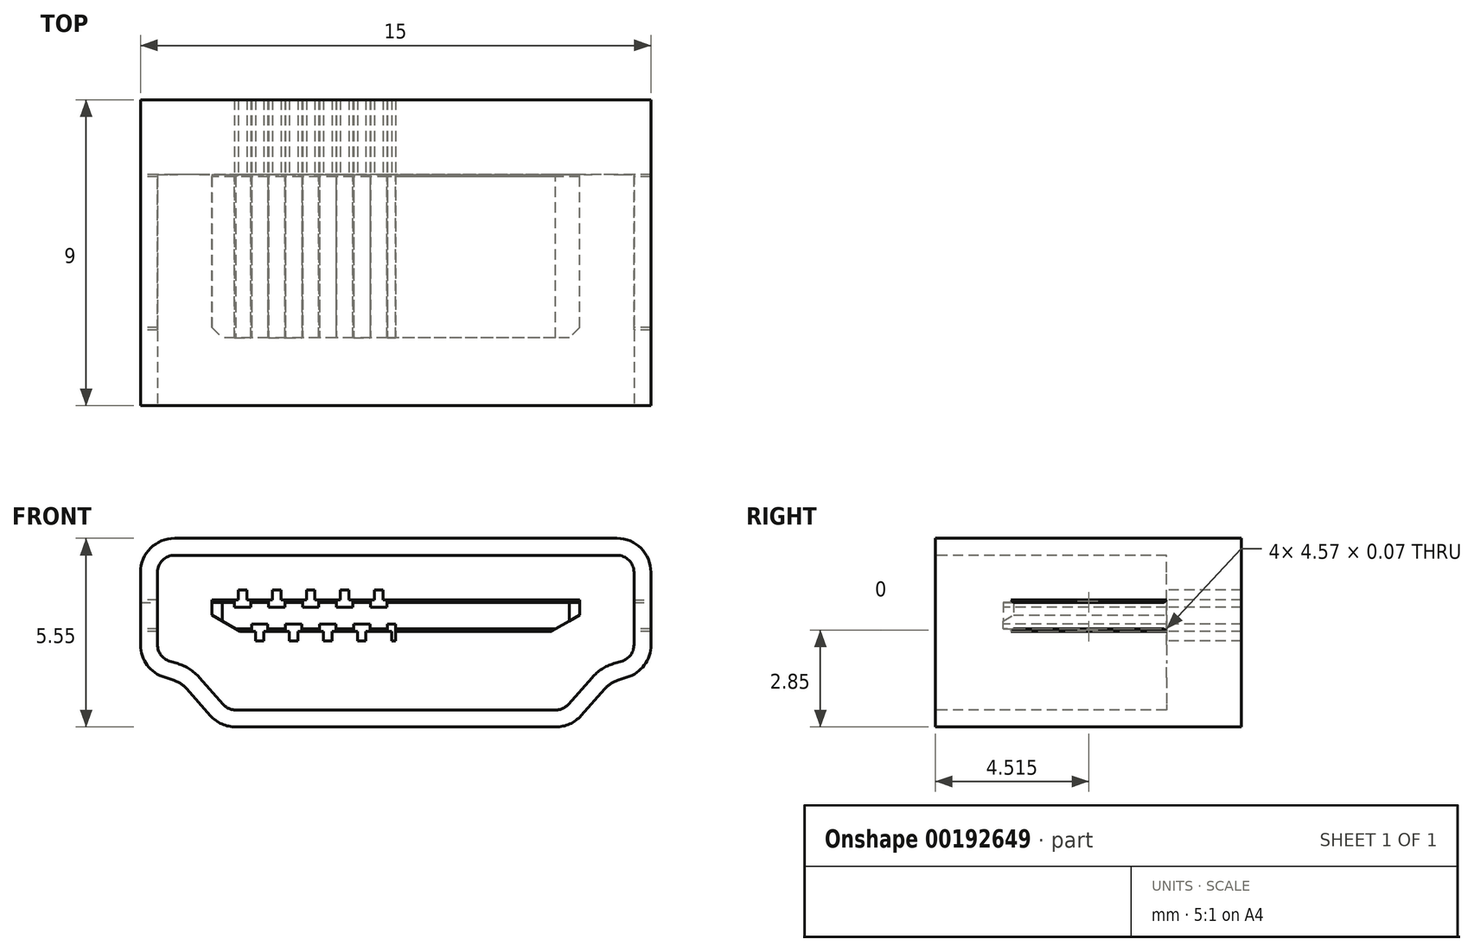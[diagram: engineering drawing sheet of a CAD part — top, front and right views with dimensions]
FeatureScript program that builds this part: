
annotation { "Feature Type Name" : "Feature", "Feature Type Description" : "" }
export const myFeature = defineFeature(function(context is Context, id is Id, definition is map)
    precondition{}
    {
        {
            var Q0;
            Q0=qCreatedBy(makeId("Front.planeOp"),FACE);
            var sketch = newSketch(context, id + "F0", { "sketchPlane" : qUnion([Q0])});
            skLineSegment(sketch, "E0", {"start": v(-6.5, 5.55) * mm, "end": v(7.5, 5.55) * mm});
            skLineSegment(sketch, "E1", {"start": v(-4.7, 0) * mm, "end": v(4.7, 0) * mm});
            skLineSegment(sketch, "E2", {"start": v(-7.5, 4.55) * mm, "end": v(-7.5, 2.42) * mm});
            skPoint(sketch, "E3.visualSharp", {"position": v(-7.5, 5.55) * mm});
            skArc(sketch, "E3.filletArc", {"start": v(-6.5, 5.55) * mm, "mid": v(-7.2, 5.26) * mm, "end": v(-7.5, 4.55) * mm});
            skArc(sketch, "E4", {"start": v(-7.5, 2.42) * mm, "mid": v(-7.3, 1.82) * mm, "end": v(-6.8, 1.46) * mm});
            skLineSegment(sketch, "E5", {"start": v(-6.8, 1.46) * mm, "end": v(-6.56, 1.39) * mm});
            skArc(sketch, "E6", {"start": v(-5.45, 0.34) * mm, "mid": v(-5.11, 0.09) * mm, "end": v(-4.7, 0) * mm});
            skLineSegment(sketch, "E7", {"start": v(-5.45, 0.34) * mm, "end": v(-6.14, 1.12) * mm});
            skArc(sketch, "E8", {"start": v(-6.14, 1.12) * mm, "mid": v(-6.33, 1.28) * mm, "end": v(-6.56, 1.39) * mm});
            skLineSegment(sketch, "E9", {"start": v(0, 0) * mm, "end": v(0, 5.55) * mm, "construction": true});
            skLineSegment(sketch, "E10.MirrorCS", {"start": v(6.8, 1.46) * mm, "end": v(6.56, 1.39) * mm});
            skArc(sketch, "E11.MirrorCS", {"start": v(5.45, 0.34) * mm, "mid": v(5.11, 0.09) * mm, "end": v(4.7, 0) * mm});
            skArc(sketch, "E12.MirrorCS", {"start": v(6.14, 1.12) * mm, "mid": v(6.33, 1.28) * mm, "end": v(6.56, 1.39) * mm});
            skLineSegment(sketch, "E13.MirrorCS", {"start": v(5.45, 0.34) * mm, "end": v(6.14, 1.12) * mm});
            skArc(sketch, "E14.MirrorCS", {"start": v(6.5, 5.55) * mm, "mid": v(7.2, 5.26) * mm, "end": v(7.5, 4.55) * mm});
            skArc(sketch, "E15.MirrorCS", {"start": v(7.5, 2.42) * mm, "mid": v(7.3, 1.82) * mm, "end": v(6.8, 1.46) * mm});
            skLineSegment(sketch, "E16.MirrorCS", {"start": v(7.5, 4.55) * mm, "end": v(7.5, 2.42) * mm});
            skSolve(sketch);
        }
        {
            var Q0;
            Q0 = qSketchRegion(id + "F0", true);
            extrude(context, id + "F1", {"entities" : qUnion([Q0]), "endBound" : BoundingType.SYMMETRIC, "depth" : 9 * mm});
        }
        {
            var Q0;
            Q0=makeQuery(id+"F1.opExtrude","CAP_FACE",FACE,{"disambiguationData":[OSD([sQuery(id+"F0.wireOp",EDGE,"E0"),sQuery(id+"F0.wireOp",EDGE,"E1"),sQuery(id+"F0.wireOp",EDGE,"E2"),sQuery(id+"F0.wireOp",EDGE,"E3.filletArc"),sQuery(id+"F0.wireOp",EDGE,"E4"),sQuery(id+"F0.wireOp",EDGE,"E5"),sQuery(id+"F0.wireOp",EDGE,"E6"),sQuery(id+"F0.wireOp",EDGE,"E7"),sQuery(id+"F0.wireOp",EDGE,"E8"),sQuery(id+"F0.wireOp",EDGE,"E10.MirrorCS"),sQuery(id+"F0.wireOp",EDGE,"E11.MirrorCS"),sQuery(id+"F0.wireOp",EDGE,"E12.MirrorCS"),sQuery(id+"F0.wireOp",EDGE,"E13.MirrorCS"),sQuery(id+"F0.wireOp",EDGE,"E14.MirrorCS"),sQuery(id+"F0.wireOp",EDGE,"E15.MirrorCS"),sQuery(id+"F0.wireOp",EDGE,"E16.MirrorCS")])],"isStart":false});
            var sketch = newSketch(context, id + "F2", { "sketchPlane" : qUnion([Q0])});
            skArc(sketch, "E17.0", {"start": v(7, 4.55) * mm, "mid": v(6.85, 4.9) * mm, "end": v(6.5, 5.05) * mm});
            skLineSegment(sketch, "E17.1", {"start": v(7, 2.42) * mm, "end": v(7, 4.55) * mm});
            skArc(sketch, "E17.2", {"start": v(6.65, 1.94) * mm, "mid": v(6.9, 2.12) * mm, "end": v(7, 2.42) * mm});
            skLineSegment(sketch, "E17.3", {"start": v(6.41, 1.87) * mm, "end": v(6.65, 1.94) * mm});
            skArc(sketch, "E17.4", {"start": v(5.77, 1.45) * mm, "mid": v(6.06, 1.7) * mm, "end": v(6.41, 1.87) * mm});
            skLineSegment(sketch, "E17.5", {"start": v(-6.65, 1.94) * mm, "end": v(-6.41, 1.87) * mm});
            skArc(sketch, "E17.6", {"start": v(-7, 2.42) * mm, "mid": v(-6.9, 2.12) * mm, "end": v(-6.65, 1.94) * mm});
            skLineSegment(sketch, "E17.7", {"start": v(-7, 4.55) * mm, "end": v(-7, 2.42) * mm});
            skArc(sketch, "E17.8", {"start": v(-6.5, 5.05) * mm, "mid": v(-6.85, 4.9) * mm, "end": v(-7, 4.55) * mm});
            skArc(sketch, "E17.9", {"start": v(-6.41, 1.87) * mm, "mid": v(-6.06, 1.7) * mm, "end": v(-5.77, 1.45) * mm});
            skLineSegment(sketch, "E17.10", {"start": v(-5.77, 1.45) * mm, "end": v(-5.08, 0.67) * mm});
            skArc(sketch, "E17.11", {"start": v(-5.08, 0.67) * mm, "mid": v(-4.9, 0.54) * mm, "end": v(-4.7, 0.5) * mm});
            skLineSegment(sketch, "E17.12", {"start": v(-4.7, 0.5) * mm, "end": v(4.7, 0.5) * mm});
            skArc(sketch, "E17.13", {"start": v(4.7, 0.5) * mm, "mid": v(4.9, 0.54) * mm, "end": v(5.08, 0.67) * mm});
            skLineSegment(sketch, "E17.14", {"start": v(6.5, 5.05) * mm, "end": v(-6.5, 5.05) * mm});
            skLineSegment(sketch, "E17.15", {"start": v(5.08, 0.67) * mm, "end": v(5.77, 1.45) * mm});
            skSolve(sketch);
        }
        {
            var Q0;
            Q0 = qSketchRegion(id + "F2", true);
            extrude(context, id + "F3", {"entities" : qUnion([Q0]), "operationType" : NewBodyOperationType.REMOVE, "oppositeDirection" : true, "depth" : 6.8 * mm});
        }
        {
            var Q0;
            Q0=makeQuery(id+"F3.boolean.opBoolean","COPY",FACE,{"derivedFrom":makeQuery(id+"F3.opExtrude","CAP_FACE",FACE,{"disambiguationData":[OSD([sQuery(id+"F2.wireOp",EDGE,"E17.0"),sQuery(id+"F2.wireOp",EDGE,"E17.1"),sQuery(id+"F2.wireOp",EDGE,"E17.2"),sQuery(id+"F2.wireOp",EDGE,"E17.3"),sQuery(id+"F2.wireOp",EDGE,"E17.4"),sQuery(id+"F2.wireOp",EDGE,"E17.5"),sQuery(id+"F2.wireOp",EDGE,"E17.6"),sQuery(id+"F2.wireOp",EDGE,"E17.7"),sQuery(id+"F2.wireOp",EDGE,"E17.8"),sQuery(id+"F2.wireOp",EDGE,"E17.9"),sQuery(id+"F2.wireOp",EDGE,"E17.10"),sQuery(id+"F2.wireOp",EDGE,"E17.11"),sQuery(id+"F2.wireOp",EDGE,"E17.12"),sQuery(id+"F2.wireOp",EDGE,"E17.13"),sQuery(id+"F2.wireOp",EDGE,"E17.14"),sQuery(id+"F2.wireOp",EDGE,"E17.15")])],"isStart":false})});
            var sketch = newSketch(context, id + "F4", { "sketchPlane" : qUnion([Q0])});
            skLineSegment(sketch, "E18", {"start": v(5.4, 3.66) * mm, "end": v(5.4, 3.29) * mm});
            skLineSegment(sketch, "E19", {"start": v(-5.4, 3.66) * mm, "end": v(-5.4, 3.29) * mm});
            skLineSegment(sketch, "E20", {"start": v(-5.4, 3.29) * mm, "end": v(-4.7, 2.88) * mm});
            skLineSegment(sketch, "E21", {"start": v(-4.7, 2.88) * mm, "end": v(4.7, 2.88) * mm});
            skLineSegment(sketch, "E22.MirrorCS", {"start": v(5.4, 3.29) * mm, "end": v(4.7, 2.88) * mm});
            skLineSegment(sketch, "E23", {"start": v(5.4, 3.67) * mm, "end": v(-5.4, 3.66) * mm});
            skLineSegment(sketch, "E24", {"start": v(-5.4, 3.66) * mm, "end": v(-5.4, 3.73) * mm});
            skLineSegment(sketch, "E25", {"start": v(-5.4, 3.73) * mm, "end": v(5.4, 3.73) * mm});
            skLineSegment(sketch, "E26", {"start": v(5.4, 3.73) * mm, "end": v(5.4, 3.67) * mm});
            skLineSegment(sketch, "E27", {"start": v(4.7, 2.88) * mm, "end": v(4.58, 2.81) * mm});
            skLineSegment(sketch, "E28", {"start": v(4.58, 2.81) * mm, "end": v(-4.58, 2.81) * mm});
            skLineSegment(sketch, "E29", {"start": v(-4.58, 2.81) * mm, "end": v(-4.7, 2.88) * mm});
            skSolve(sketch);
        }
        {
            var Q0;
            Q0 = qSketchRegion(id + "F4", true);
            extrude(context, id + "F11", {"entities" : qUnion([Q0]), "depth" : 4.8 * mm});
        }
        {
            var Q0;
            Q0=qCreatedBy(makeId("Right.planeOp"),FACE);
            var sketch = newSketch(context, id + "F5", { "sketchPlane" : qUnion([Q0])});
            skLineSegment(sketch, "E30", {"start": v(2.3, 3.73) * mm, "end": v(2.23, 3.67) * mm});
            skLineSegment(sketch, "E31", {"start": v(2.23, 3.67) * mm, "end": v(-2.5, 3.67) * mm});
            skLineSegment(sketch, "E32", {"start": v(-2.5, 3.67) * mm, "end": v(-2.5, 3.73) * mm});
            skLineSegment(sketch, "E33", {"start": v(-2.5, 3.73) * mm, "end": v(2.3, 3.73) * mm});
            skLineSegment(sketch, "E34", {"start": v(-2.5, 2.88) * mm, "end": v(-2.5, 2.81) * mm});
            skLineSegment(sketch, "E35", {"start": v(-2.5, 2.81) * mm, "end": v(2.3, 2.81) * mm});
            skLineSegment(sketch, "E36", {"start": v(2.3, 2.81) * mm, "end": v(2.23, 2.88) * mm});
            skLineSegment(sketch, "E37", {"start": v(2.23, 2.88) * mm, "end": v(-2.5, 2.88) * mm});
            skSolve(sketch);
        }
        {
            var Q0;
            Q0 = qSketchRegion(id + "F5", true);
            extrude(context, id + "F6", {"entities" : qUnion([Q0]), "operationType" : NewBodyOperationType.REMOVE, "endBound" : BoundingType.THROUGH_ALL, "depth" : 10.8 * mm, "hasSecondDirection" : true, "secondDirectionBound" : SecondDirectionBoundingType.THROUGH_ALL, "secondDirectionOppositeDirection" : true, "secondDirectionDepth" : 25.4 * mm});
        }
        {
            var Q0;
            Q0=makeQuery(id+"F6.boolean.opBoolean","COPY",EDGE,{"derivedFrom":makeQuery(id+"F6.opExtrude","SWEPT_EDGE",EDGE,{"disambiguationData":[OSD([sQuery(id+"F5.wireOp",EDGE,"E31"),sQuery(id+"F5.wireOp",EDGE,"E32")])]})});
            var Q1;
            Q1=makeQuery(id+"F6.boolean.opBoolean","COPY",EDGE,{"derivedFrom":makeQuery(id+"F6.opExtrude","SWEPT_EDGE",EDGE,{"disambiguationData":[OSD([sQuery(id+"F5.wireOp",EDGE,"E34"),sQuery(id+"F5.wireOp",EDGE,"E37")])]})});
            var Q2;
            Q2=makeQuery(id+"F11.opExtrude","CAP_EDGE",EDGE,{"disambiguationData":[OSD([sQuery(id+"F4.wireOp",EDGE,"E18"),sQuery(id+"F4.wireOp",EDGE,"E26")])],"isStart":false});
            var Q3;
            Q3=makeQuery(id+"F11.opExtrude","CAP_EDGE",EDGE,{"disambiguationData":[OSD([sQuery(id+"F4.wireOp",EDGE,"E19"),sQuery(id+"F4.wireOp",EDGE,"E24")])],"isStart":false});
            chamfer(context, id + "F7", {"entities" : qUnion([Q0, Q1, Q2, Q3]), "width" : .3 * mm, "tangentPropagation" : true});
        }
        {
            var Q0;
            Q0=makeQuery(id+"F11.opExtrude","CAP_FACE",FACE,{"disambiguationData":[OSD([sQuery(id+"F4.wireOp",EDGE,"E18"),sQuery(id+"F4.wireOp",EDGE,"E19"),sQuery(id+"F4.wireOp",EDGE,"E20"),sQuery(id+"F4.wireOp",EDGE,"E22.MirrorCS"),sQuery(id+"F4.wireOp",EDGE,"E24"),sQuery(id+"F4.wireOp",EDGE,"E25"),sQuery(id+"F4.wireOp",EDGE,"E26"),sQuery(id+"F4.wireOp",EDGE,"E27"),sQuery(id+"F4.wireOp",EDGE,"E28"),sQuery(id+"F4.wireOp",EDGE,"E29")])],"isStart":false});
            var sketch = newSketch(context, id + "F8", { "sketchPlane" : qUnion([Q0])});
            skLineSegment(sketch, "E38.bottom", {"start": v(-4.74, 3.73) * mm, "end": v(-4.63, 3.73) * mm});
            skLineSegment(sketch, "E38.top", {"start": v(-4.74, 3.52) * mm, "end": v(-4.26, 3.52) * mm});
            skLineSegment(sketch, "E38.left", {"start": v(-4.74, 3.73) * mm, "end": v(-4.74, 3.52) * mm});
            skLineSegment(sketch, "E38.right", {"start": v(-4.26, 3.73) * mm, "end": v(-4.26, 3.52) * mm});
            skPoint(sketch, "E38.middle", {"position": v(-4.5, 3.63) * mm});
            skLineSegment(sketch, "E39.bottom", {"start": v(-3.74, 3.73) * mm, "end": v(-3.62, 3.73) * mm});
            skLineSegment(sketch, "E39.top", {"start": v(-3.74, 3.52) * mm, "end": v(-3.26, 3.52) * mm});
            skLineSegment(sketch, "E39.left", {"start": v(-3.74, 3.73) * mm, "end": v(-3.74, 3.52) * mm});
            skLineSegment(sketch, "E39.right", {"start": v(-3.26, 3.73) * mm, "end": v(-3.26, 3.52) * mm});
            skPoint(sketch, "E39.middle", {"position": v(-3.5, 3.63) * mm});
            skLineSegment(sketch, "E40.bottom", {"start": v(-3.76, 2.81) * mm, "end": v(-3.88, 2.81) * mm});
            skLineSegment(sketch, "E40.top", {"start": v(-3.76, 3.02) * mm, "end": v(-4.24, 3.02) * mm});
            skLineSegment(sketch, "E40.left", {"start": v(-3.76, 2.81) * mm, "end": v(-3.76, 3.02) * mm});
            skLineSegment(sketch, "E40.right", {"start": v(-4.24, 2.81) * mm, "end": v(-4.24, 3.02) * mm});
            skPoint(sketch, "E40.middle", {"position": v(-4, 2.92) * mm});
            skLineSegment(sketch, "E41", {"start": v(-4.5, 3.63) * mm, "end": v(-3.5, 3.63) * mm, "construction": true});
            skLineSegment(sketch, "E42", {"start": v(-4, 3.63) * mm, "end": v(-4, 2.92) * mm, "construction": true});
            skLineSegment(sketch, "E43", {"start": v(-4.63, 3.73) * mm, "end": v(-4.63, 4.03) * mm});
            skLineSegment(sketch, "E44", {"start": v(-4.63, 4.03) * mm, "end": v(-4.38, 4.03) * mm});
            skLineSegment(sketch, "E45", {"start": v(-4.38, 4.03) * mm, "end": v(-4.38, 3.73) * mm});
            skLineSegment(sketch, "E46.trimOffspring", {"start": v(-4.38, 3.73) * mm, "end": v(-4.26, 3.73) * mm});
            skLineSegment(sketch, "E47.MirrorCS", {"start": v(-3.62, 4.03) * mm, "end": v(-3.62, 3.73) * mm});
            skLineSegment(sketch, "E48.MirrorCS", {"start": v(-3.38, 4.03) * mm, "end": v(-3.62, 4.03) * mm});
            skLineSegment(sketch, "E49.MirrorCS", {"start": v(-3.38, 3.73) * mm, "end": v(-3.38, 4.03) * mm});
            skLineSegment(sketch, "E50.trimOffspring", {"start": v(-3.38, 3.73) * mm, "end": v(-3.26, 3.73) * mm});
            skLineSegment(sketch, "E51", {"start": v(-4.12, 2.81) * mm, "end": v(-4.12, 2.52) * mm});
            skLineSegment(sketch, "E52", {"start": v(-4.13, 2.52) * mm, "end": v(-3.88, 2.52) * mm});
            skLineSegment(sketch, "E53", {"start": v(-3.88, 2.52) * mm, "end": v(-3.88, 2.81) * mm});
            skLineSegment(sketch, "E54.trimOffspring", {"start": v(-4.13, 2.81) * mm, "end": v(-4.24, 2.81) * mm});
            skLineSegment(sketch, "E55", {"start": v(-3.5, 3.63) * mm, "end": v(-3.5, 3.18) * mm, "construction": true});
            skLineSegment(sketch, "E56.MirrorCS", {"start": v(-3.24, 2.81) * mm, "end": v(-3.12, 2.81) * mm});
            skLineSegment(sketch, "E57.MirrorCS", {"start": v(-2.87, 2.81) * mm, "end": v(-2.76, 2.81) * mm});
            skLineSegment(sketch, "E58.MirrorCS", {"start": v(-2.87, 2.81) * mm, "end": v(-2.87, 2.52) * mm});
            skLineSegment(sketch, "E59.MirrorCS", {"start": v(-2.76, 2.81) * mm, "end": v(-2.76, 3.02) * mm});
            skPoint(sketch, "E60.MirrorP", {"position": v(-3, 2.92) * mm});
            skLineSegment(sketch, "E61.MirrorCS", {"start": v(-3.12, 2.52) * mm, "end": v(-3.12, 2.81) * mm});
            skLineSegment(sketch, "E62.MirrorCS", {"start": v(-3, 3.63) * mm, "end": v(-3, 2.92) * mm, "construction": true});
            skLineSegment(sketch, "E63.MirrorCS", {"start": v(-3.24, 3.02) * mm, "end": v(-2.76, 3.02) * mm});
            skLineSegment(sketch, "E64.MirrorCS", {"start": v(-2.87, 2.52) * mm, "end": v(-3.12, 2.52) * mm});
            skLineSegment(sketch, "E65.MirrorCS", {"start": v(-3.24, 2.81) * mm, "end": v(-3.24, 3.02) * mm});
            skLineSegment(sketch, "E66.MirrorCS", {"start": v(-2.62, 3.73) * mm, "end": v(-2.74, 3.73) * mm});
            skLineSegment(sketch, "E67.MirrorCS", {"start": v(-2.26, 3.73) * mm, "end": v(-2.37, 3.73) * mm});
            skLineSegment(sketch, "E68.MirrorCS", {"start": v(-2.26, 3.52) * mm, "end": v(-2.74, 3.52) * mm});
            skLineSegment(sketch, "E69.MirrorCS", {"start": v(-2.37, 3.73) * mm, "end": v(-2.37, 4.03) * mm});
            skLineSegment(sketch, "E70.MirrorCS", {"start": v(-2.26, 3.73) * mm, "end": v(-2.26, 3.52) * mm});
            skLineSegment(sketch, "E71.MirrorCS", {"start": v(-2.62, 4.03) * mm, "end": v(-2.62, 3.73) * mm});
            skLineSegment(sketch, "E72.MirrorCS", {"start": v(-2.37, 4.03) * mm, "end": v(-2.62, 4.03) * mm});
            skPoint(sketch, "E73.MirrorP", {"position": v(-2.5, 3.63) * mm});
            skLineSegment(sketch, "E74.MirrorCS", {"start": v(-2.74, 3.73) * mm, "end": v(-2.74, 3.52) * mm});
            skLineSegment(sketch, "E75", {"start": v(-2.5, 3.63) * mm, "end": v(-2.5, 3.18) * mm, "construction": true});
            skLineSegment(sketch, "E76.MirrorCS", {"start": v(-1.76, 2.81) * mm, "end": v(-1.87, 2.81) * mm});
            skLineSegment(sketch, "E77.MirrorCS", {"start": v(-0.87, 2.81) * mm, "end": v(-0.76, 2.81) * mm});
            skLineSegment(sketch, "E78.MirrorCS", {"start": v(-1.24, 2.81) * mm, "end": v(-1.12, 2.81) * mm});
            skLineSegment(sketch, "E79.MirrorCS", {"start": v(-2.12, 2.81) * mm, "end": v(-2.24, 2.81) * mm});
            skPoint(sketch, "E80.MirrorP", {"position": v(-2, 2.92) * mm});
            skLineSegment(sketch, "E81.MirrorCS", {"start": v(-1.76, 3.02) * mm, "end": v(-2.24, 3.02) * mm});
            skLineSegment(sketch, "E82.MirrorCS", {"start": v(-0.76, 2.81) * mm, "end": v(-0.76, 3.02) * mm});
            skLineSegment(sketch, "E83.MirrorCS", {"start": v(-1.24, 2.81) * mm, "end": v(-1.24, 3.02) * mm});
            skLineSegment(sketch, "E84.MirrorCS", {"start": v(-0.87, 2.52) * mm, "end": v(-1.12, 2.52) * mm});
            skLineSegment(sketch, "E85.MirrorCS", {"start": v(-2.24, 2.81) * mm, "end": v(-2.24, 3.02) * mm});
            skPoint(sketch, "E86.MirrorP", {"position": v(-1, 2.92) * mm});
            skLineSegment(sketch, "E87.MirrorCS", {"start": v(-1.87, 2.52) * mm, "end": v(-1.87, 2.81) * mm});
            skLineSegment(sketch, "E88.MirrorCS", {"start": v(-0.87, 2.81) * mm, "end": v(-0.87, 2.52) * mm});
            skLineSegment(sketch, "E89.MirrorCS", {"start": v(-1.76, 2.81) * mm, "end": v(-1.76, 3.02) * mm});
            skLineSegment(sketch, "E90.MirrorCS", {"start": v(-2.12, 2.52) * mm, "end": v(-1.87, 2.52) * mm});
            skLineSegment(sketch, "E91.MirrorCS", {"start": v(-1.12, 2.52) * mm, "end": v(-1.12, 2.81) * mm});
            skLineSegment(sketch, "E92.MirrorCS", {"start": v(-1.24, 3.02) * mm, "end": v(-0.76, 3.02) * mm});
            skLineSegment(sketch, "E93.MirrorCS", {"start": v(-2.12, 2.81) * mm, "end": v(-2.12, 2.52) * mm});
            skLineSegment(sketch, "E94.MirrorCS", {"start": v(-1.62, 4.03) * mm, "end": v(-1.37, 4.03) * mm});
            skLineSegment(sketch, "E95.MirrorCS", {"start": v(-1.62, 3.73) * mm, "end": v(-1.62, 4.03) * mm});
            skLineSegment(sketch, "E96.MirrorCS", {"start": v(-1.37, 4.03) * mm, "end": v(-1.37, 3.73) * mm});
            skLineSegment(sketch, "E97.MirrorCS", {"start": v(-1.26, 3.73) * mm, "end": v(-1.37, 3.73) * mm});
            skLineSegment(sketch, "E98.MirrorCS", {"start": v(-1.62, 3.73) * mm, "end": v(-1.74, 3.73) * mm});
            skLineSegment(sketch, "E99.MirrorCS", {"start": v(-1.74, 3.73) * mm, "end": v(-1.74, 3.52) * mm});
            skLineSegment(sketch, "E100.MirrorCS", {"start": v(-1.26, 3.52) * mm, "end": v(-1.74, 3.52) * mm});
            skLineSegment(sketch, "E101.MirrorCS", {"start": v(-1.26, 3.73) * mm, "end": v(-1.26, 3.52) * mm});
            skLineSegment(sketch, "E102.MirrorCS", {"start": v(-0.74, 3.73) * mm, "end": v(-0.74, 3.52) * mm});
            skLineSegment(sketch, "E103.MirrorCS", {"start": v(-0.26, 3.52) * mm, "end": v(-0.74, 3.52) * mm});
            skLineSegment(sketch, "E104.MirrorCS", {"start": v(-0.26, 3.73) * mm, "end": v(-0.26, 3.52) * mm});
            skLineSegment(sketch, "E105.MirrorCS", {"start": v(-0.26, 3.73) * mm, "end": v(-0.37, 3.73) * mm});
            skLineSegment(sketch, "E106.MirrorCS", {"start": v(-0.37, 3.73) * mm, "end": v(-0.37, 4.03) * mm});
            skLineSegment(sketch, "E107.MirrorCS", {"start": v(-0.62, 4.03) * mm, "end": v(-0.62, 3.73) * mm});
            skLineSegment(sketch, "E108.MirrorCS", {"start": v(-0.37, 4.03) * mm, "end": v(-0.62, 4.03) * mm});
            skLineSegment(sketch, "E109.MirrorCS", {"start": v(-0.62, 3.73) * mm, "end": v(-0.74, 3.73) * mm});
            skLineSegment(sketch, "E110", {"start": v(0, 2.52) * mm, "end": v(-0.13, 2.52) * mm});
            skLineSegment(sketch, "E111", {"start": v(-0.13, 2.52) * mm, "end": v(-0.13, 2.81) * mm});
            skLineSegment(sketch, "E112", {"start": v(-0.13, 2.81) * mm, "end": v(-0.24, 2.81) * mm});
            skLineSegment(sketch, "E113", {"start": v(-0.24, 2.81) * mm, "end": v(-0.24, 3.02) * mm});
            skLineSegment(sketch, "E114", {"start": v(-0.24, 3.02) * mm, "end": v(0, 3.02) * mm});
            skLineSegment(sketch, "E115", {"start": v(0, 3.02) * mm, "end": v(0, 2.52) * mm});
            skSolve(sketch);
        }
        {
            var Q0;
            Q0 = qSketchRegion(id + "F8", true);
            extrude(context, id + "F9", {"entities" : qUnion([Q0]), "operationType" : NewBodyOperationType.REMOVE, "endBound" : BoundingType.THROUGH_ALL, "oppositeDirection" : true, "depth" : 25.4 * mm});
        }
    });
